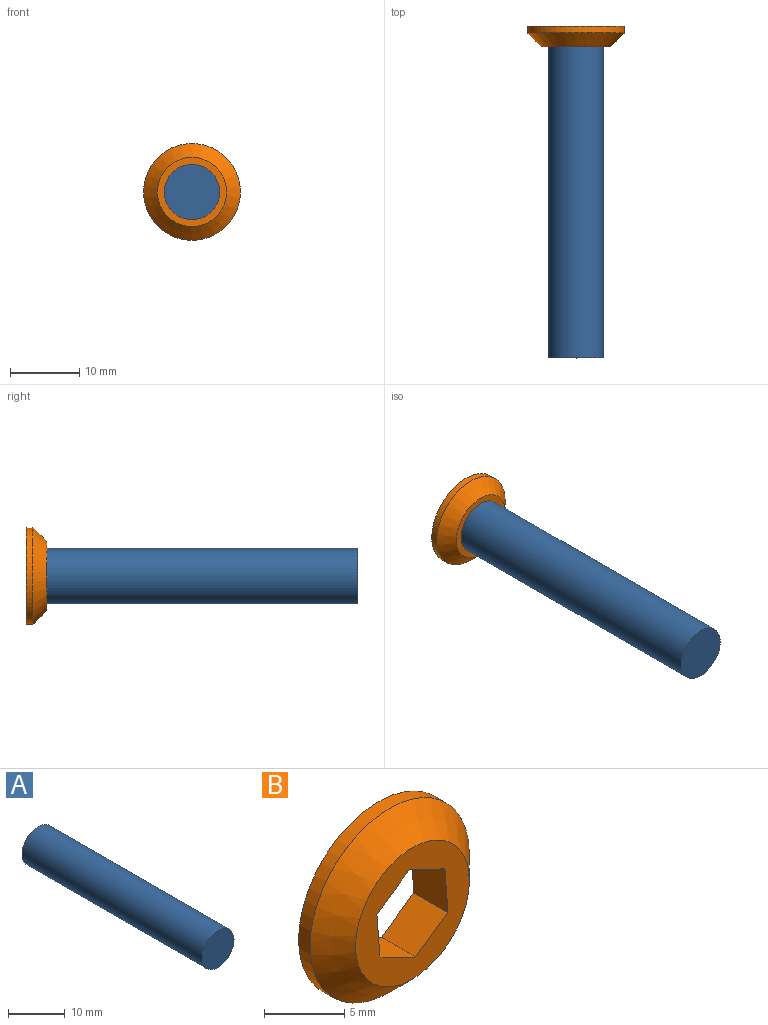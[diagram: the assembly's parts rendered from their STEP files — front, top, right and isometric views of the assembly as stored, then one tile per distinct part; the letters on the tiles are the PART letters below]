
ASSEMBLY  parts=2 mates=1
PART A: 3 faces, bbox 8x45x8 mm
  f0: cylinder r=4mm len=45mm, axis (0,1,0), area 1131mm2, adj f1,f2
  f1: plane 8x8mm, normal (0,-1,0), area 50.3mm2, adj f0
  f2: plane 8x8mm, normal (0,1,0), area 50.3mm2, adj f0
PART B: 10 faces, bbox 14x3x14 mm
  f0: plane 3x2.85mm, normal (-0.57,0,0.82), area 10.4mm2, adj f1,f6,f7,f8
  f1: plane 3.13x3mm, normal (0.43,0,0.9), area 10.4mm2, adj f0,f2,f7,f8
  f2: plane 3.45x3mm, normal (1,0,0.08), area 10.4mm2, adj f1,f3,f7,f8
  f3: plane 3x2.85mm, normal (0.57,0,-0.82), area 10.4mm2, adj f2,f4,f7,f8
  f4: plane 3.13x3mm, normal (-0.43,0,-0.9), area 10.4mm2, adj f3,f6,f7,f8
  f5: cylinder r=7mm len=14mm, axis (0,1,0), area 44mm2, adj f8,f9
  f6: plane 3.45x3mm, normal (-1,0,-0.08), area 10.4mm2, adj f0,f4,f7,f8
  f7: plane 10x10mm, normal (0,-1,0), area 47.4mm2, adj f0,f1,f2,f3,f4,f6,f9
  f8: plane 14x14mm, normal (0,1,0), area 122.8mm2, adj f0,f1,f2,f3,f4,f5,f6
  f9: cone r=5mm half-angle=45deg, axis (0,1,0), area 106.6mm2, adj f5,f7
PLACE A t=(-10.34,-2.61,-17.46)mm
PLACE B t=(-10.34,0.39,-17.46)mm
MATE fastened B.f5 <-> A.f0  axis (0,-1,0) through (-10.34,-2.61,-17.46)mm
